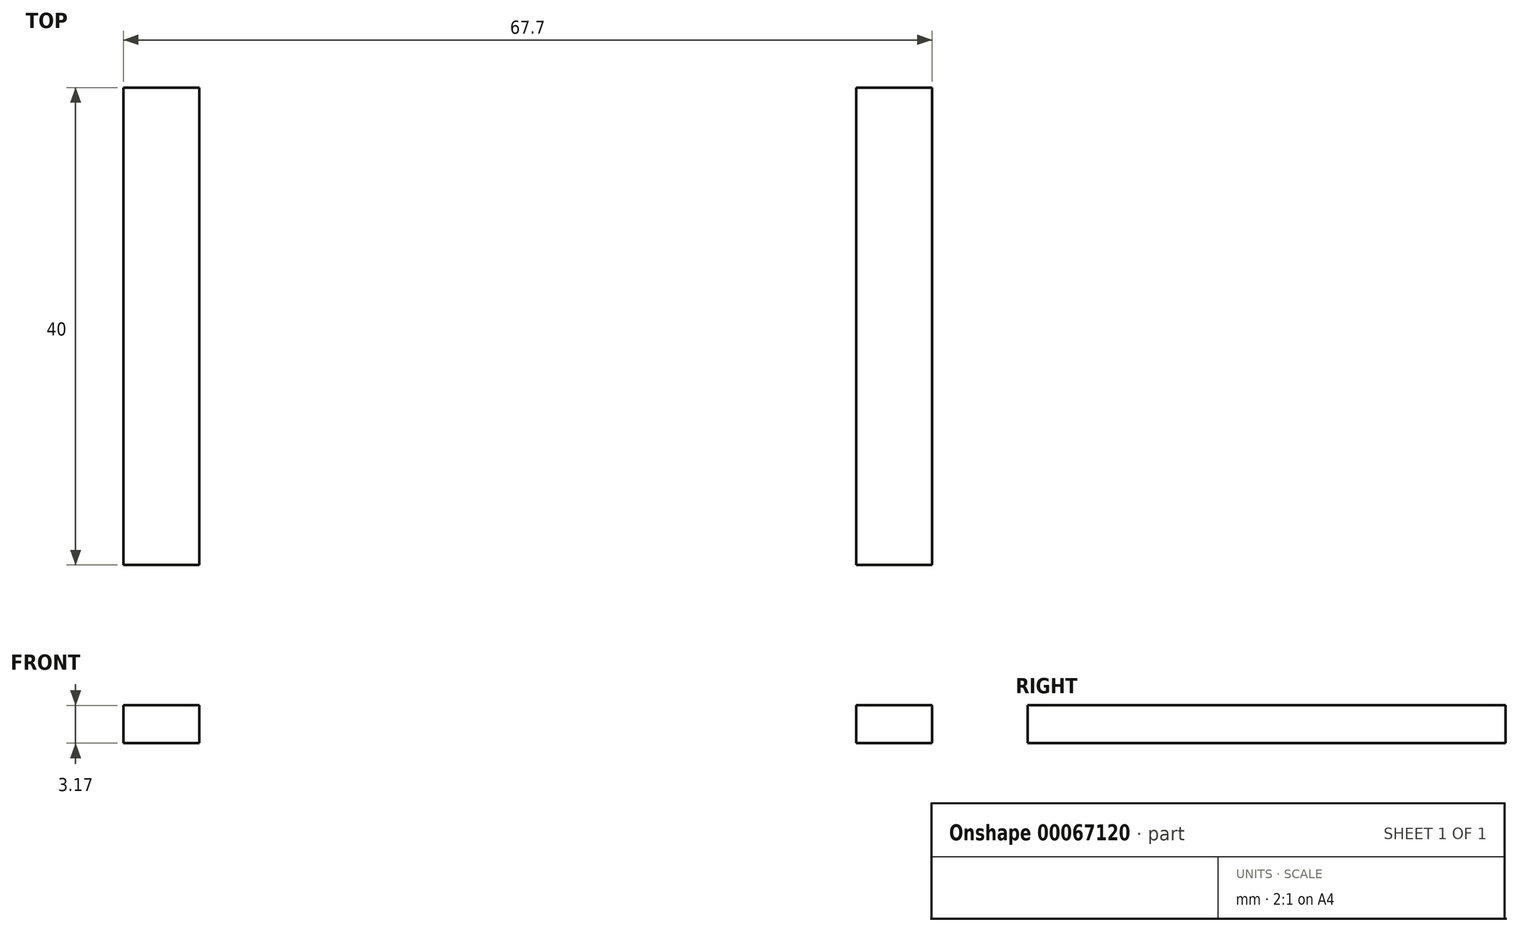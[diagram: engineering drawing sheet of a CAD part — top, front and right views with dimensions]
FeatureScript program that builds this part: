
annotation { "Feature Type Name" : "Feature", "Feature Type Description" : "" }
export const myFeature = defineFeature(function(context is Context, id is Id, definition is map)
    precondition{}
    {
        {
            var Q0;
            Q0=qCreatedBy(makeId("Top.planeOp"),FACE);
            var sketch = newSketch(context, id + "F0", { "sketchPlane" : qUnion([Q0])});
            skLineSegment(sketch, "E0.bottom", {"start": v(-27.5, 0) * mm, "end": v(27.5, 0) * mm});
            skLineSegment(sketch, "E0.top", {"start": v(-27.5, -55) * mm, "end": v(27.5, -55) * mm});
            skLineSegment(sketch, "E0.left", {"start": v(-27.5, 0) * mm, "end": v(-27.5, -55) * mm});
            skLineSegment(sketch, "E0.right", {"start": v(27.5, 0) * mm, "end": v(27.5, -55) * mm});
            skLineSegment(sketch, "E1.bottom", {"start": v(-20, 0) * mm, "end": v(20, 0) * mm});
            skLineSegment(sketch, "E1.top", {"start": v(-20, 6.35) * mm, "end": v(20, 6.35) * mm});
            skLineSegment(sketch, "E1.left", {"start": v(-20, 0) * mm, "end": v(-20, 6.35) * mm});
            skLineSegment(sketch, "E1.right", {"start": v(20, 0) * mm, "end": v(20, 6.35) * mm});
            skLineSegment(sketch, "E2.bottom", {"start": v(-27.5, -7.5) * mm, "end": v(-33.85, -7.5) * mm});
            skLineSegment(sketch, "E2.top", {"start": v(-27.5, -47.5) * mm, "end": v(-33.85, -47.5) * mm});
            skLineSegment(sketch, "E2.left", {"start": v(-27.5, -7.5) * mm, "end": v(-27.5, -47.5) * mm});
            skLineSegment(sketch, "E2.right", {"start": v(-33.85, -7.5) * mm, "end": v(-33.85, -47.5) * mm});
            skLineSegment(sketch, "E3.bottom", {"start": v(27.5, -7.5) * mm, "end": v(33.85, -7.5) * mm});
            skLineSegment(sketch, "E3.top", {"start": v(27.5, -47.5) * mm, "end": v(33.85, -47.5) * mm});
            skLineSegment(sketch, "E3.left", {"start": v(27.5, -7.5) * mm, "end": v(27.5, -47.5) * mm});
            skLineSegment(sketch, "E3.right", {"start": v(33.85, -7.5) * mm, "end": v(33.85, -47.5) * mm});
            skLineSegment(sketch, "E4.bottom", {"start": v(20, -55) * mm, "end": v(-20, -55) * mm});
            skLineSegment(sketch, "E4.top", {"start": v(20, -61.35) * mm, "end": v(-20, -61.35) * mm});
            skLineSegment(sketch, "E4.left", {"start": v(20, -55) * mm, "end": v(20, -61.35) * mm});
            skLineSegment(sketch, "E4.right", {"start": v(-20, -55) * mm, "end": v(-20, -61.35) * mm});
            skLineSegment(sketch, "E5", {"start": v(-20, 6.35) * mm, "end": v(-27.5, 0) * mm, "construction": true});
            skLineSegment(sketch, "E6", {"start": v(20, 6.35) * mm, "end": v(27.5, 0) * mm, "construction": true});
            skLineSegment(sketch, "E7", {"start": v(33.85, -7.5) * mm, "end": v(27.5, 0) * mm, "construction": true});
            skLineSegment(sketch, "E8", {"start": v(33.85, -47.5) * mm, "end": v(27.5, -55) * mm, "construction": true});
            skSolve(sketch);
        }
        {
            var Q0;
            {var subQ8=sQuery(id+"F0.wireOp",EDGE,"E1.bottom");Q0=makeQuery(id+"F0.imprint","IMPRINT",FACE,{"disambiguationData":[TD([[makeQuery(id+"F0.imprint","IMPRINT",EDGE,{"derivedFrom":subQ8}),-1.0]])]});}
            var Q1;
            Q1=makeQuery(id+"F0.imprint","IMPRINT",FACE,{"disambiguationData":[TD([[makeQuery(id+"F0.imprint","IMPRINT",EDGE,{"derivedFrom":sQuery(id+"F0.wireOp",EDGE,"E1.bottom")}),1.0]])]});
            var Q2;
            Q2=makeQuery(id+"F0.imprint","IMPRINT",FACE,{"disambiguationData":[TD([[makeQuery(id+"F0.imprint","IMPRINT",EDGE,{"derivedFrom":sQuery(id+"F0.wireOp",EDGE,"E2.bottom")}),1.0]])]});
            var Q3;
            Q3=makeQuery(id+"F0.imprint","IMPRINT",FACE,{"disambiguationData":[TD([[makeQuery(id+"F0.imprint","IMPRINT",EDGE,{"derivedFrom":sQuery(id+"F0.wireOp",EDGE,"E3.bottom")}),-1.0]])]});
            var Q4;
            Q4=makeQuery(id+"F0.imprint","IMPRINT",FACE,{"disambiguationData":[TD([[makeQuery(id+"F0.imprint","IMPRINT",EDGE,{"derivedFrom":sQuery(id+"F0.wireOp",EDGE,"E4.bottom")}),1.0]])]});
            extrude(context, id + "F1", {"entities" : qUnion([Q0, Q1, Q2, Q3, Q4]), "depth" : 3.17 * mm});
        }
    });
